# Revit family: Edelstahlrohrschelle V2A, M 8, Ø 15- 46
name_source: partatom
category: HLS-Bauteile
revit_build: Autodesk Revit 2017 (Build: 20190507_1515(x64)
units: mm (PartAtom-declared; Revit-internal decimal feet)

## family parameters
Arbeitsebenenbasiert = Ja
Beim Laden mit Abzugskörper schneiden = Nein
Bemaßung runder Anschluss = Durchmesser verwenden
Gemeinsam genutzt = Ja
Immer vertikal = Nein
Raumberechnungspunkt = Nein
Teiletyp = Normal

## types (6) — shared parameters
A = 8 mm  [stored 0.0262467 ft]
Anschluss = M8
Anschlußhöhe = 8 mm
Bauart = zweiteilig
DF1 = 13 mm
DF2 = 15 mm  [stored 0.0492126 ft]
DVS = 7 mm  [stored 0.0229659 ft]
Fabrikat = MEFA
Firma = MEFA Befestigungs- und Montagesysteme GmbH
HGA = 7 mm  [stored 0.0229659 ft]
Kurztext1 = Rohrschelle Edelstahl V2A 20x1,5
MB = 20 mm  [stored 0.0656168 ft]
MD = 2 mm  [stored 0.00656168 ft]
Material = Edelstahl
Materialmaße = 20x1,5 mm
Mengeneinheit = St
Verschluss = Schraubenverschluss
Verschluss-Schraube = M6
Vorgabe-Ansicht = 1219 mm
max. zul. Last horizontal = 0.00 kN
max. zul. Last vertikal = 0.00 kN
vpe = 50 St
zero-valued in all types: Nennweite DN Rohr, Rohraußendurchmesser, Stärke Material

## per-type parameters (varying)
| type | AB | Achsabstand | Artikelnummer | B | D | Dmax | Dmin | EAN | Gewicht | Gewicht pro Bauteil | H | Kurztext2 | R | RM | Rohraußendurchmesser Zoll | S | max. Rohraußendurchmesser | min. Rohraußendurchmesser |
| Edelstahlrohrschelle V2A, M 8, Ø 15- 20 | 5 mm  [stored 0.0164042 ft] | 36 mm | 0469175 | 51 mm  [stored 0.167323 ft] | 20 mm  [stored 0.0656168 ft] | 20 mm  [stored 0.0656168 ft] | 15 mm  [stored 0.0492126 ft] | 4250928412188 | 0.05 kg | 0.05 kg | 30 mm  [stored 0.0984252 ft] | 15 - 20 mm M8 | 10 mm  [stored 0.0328084 ft] | 12 mm  [stored 0.0393701 ft] | 3/8 Zoll | 38 mm  [stored 0.124672 ft] | 20 mm  [stored 0.0656168 ft] | 15 mm  [stored 0.0492126 ft] |
| Edelstahlrohrschelle V2A, M 8, Ø 21- 25 | 4 mm  [stored 0.0131234 ft] | 43 mm | 0469176 | 56 mm | 25 mm  [stored 0.082021 ft] | 25 mm  [stored 0.082021 ft] | 21 mm  [stored 0.0688976 ft] | 4250928412195 | 0.05 kg | 0.05 kg | 35 mm  [stored 0.114829 ft] | 21 - 25 mm M8 | 13 mm | 14 mm  [stored 0.0459318 ft] | 1/2 Zoll | 43 mm  [stored 0.141076 ft] | 25 mm  [stored 0.082021 ft] | 21 mm  [stored 0.0688976 ft] |
| Edelstahlrohrschelle V2A, M 8, Ø 26- 30 | 4 mm  [stored 0.0131234 ft] | 48 mm | 0469177 | 61 mm | 30 mm  [stored 0.0984252 ft] | 30 mm  [stored 0.0984252 ft] | 26 mm | 4250928412201 | 0.06 kg | 0.06 kg | 40 mm  [stored 0.131234 ft] | 26 - 30 mm M8 | 15 mm  [stored 0.0492126 ft] | 17 mm | 3/4 Zoll | 48 mm  [stored 0.15748 ft] | 30 mm  [stored 0.0984252 ft] | 26 mm |
| Edelstahlrohrschelle V2A, M 8, Ø 31- 35 | 4 mm  [stored 0.0131234 ft] | 53 mm | 0469178 | 66 mm  [stored 0.216535 ft] | 35 mm  [stored 0.114829 ft] | 35 mm  [stored 0.114829 ft] | 31 mm  [stored 0.101706 ft] | 4250928412218 | 0.06 kg | 0.06 kg | 45 mm | 31 - 35 mm M8 | 18 mm  [stored 0.0590551 ft] | 19 mm  [stored 0.062336 ft] | 1 Zoll | 53 mm  [stored 0.173885 ft] | 35 mm  [stored 0.114829 ft] | 31 mm  [stored 0.101706 ft] |
| Edelstahlrohrschelle V2A, M 8, Ø 36- 40 | 4 mm  [stored 0.0131234 ft] | 59 mm | 0469171 | 71 mm  [stored 0.23294 ft] | 40 mm  [stored 0.131234 ft] | 40 mm  [stored 0.131234 ft] | 36 mm  [stored 0.11811 ft] | 4250928412171 | 0.06 kg | 0.06 kg | 50 mm  [stored 0.164042 ft] | 36 - 40 mm M8 | 20 mm  [stored 0.0656168 ft] | 22 mm  [stored 0.0721785 ft] | Zoll | 58 mm  [stored 0.190289 ft] | 40 mm  [stored 0.131234 ft] | 36 mm  [stored 0.11811 ft] |
| Edelstahlrohrschelle,V2A, M 8, Ø 41- 46 | 5 mm  [stored 0.0164042 ft] | 65 mm | 0469170 | 77 mm | 46 mm  [stored 0.150919 ft] | 46 mm  [stored 0.150919 ft] | 41 mm  [stored 0.134514 ft] | 4250928412164 | 0.07 kg | 0.07 kg | 56 mm | 41 - 46 mm M8 | 23 mm  [stored 0.0754593 ft] | 25 mm  [stored 0.082021 ft] | 1 1/4 Zoll | 64 mm  [stored 0.209974 ft] | 46 mm  [stored 0.150919 ft] | 41 mm  [stored 0.134514 ft] |

note: [stored X ft] marks values corroborated as IEEE doubles in the binary element streams (Revit-internal decimal feet)

## geometry (parser evidence)
native form markers: Sweep x4
no freeform markers — native parametric forms only
